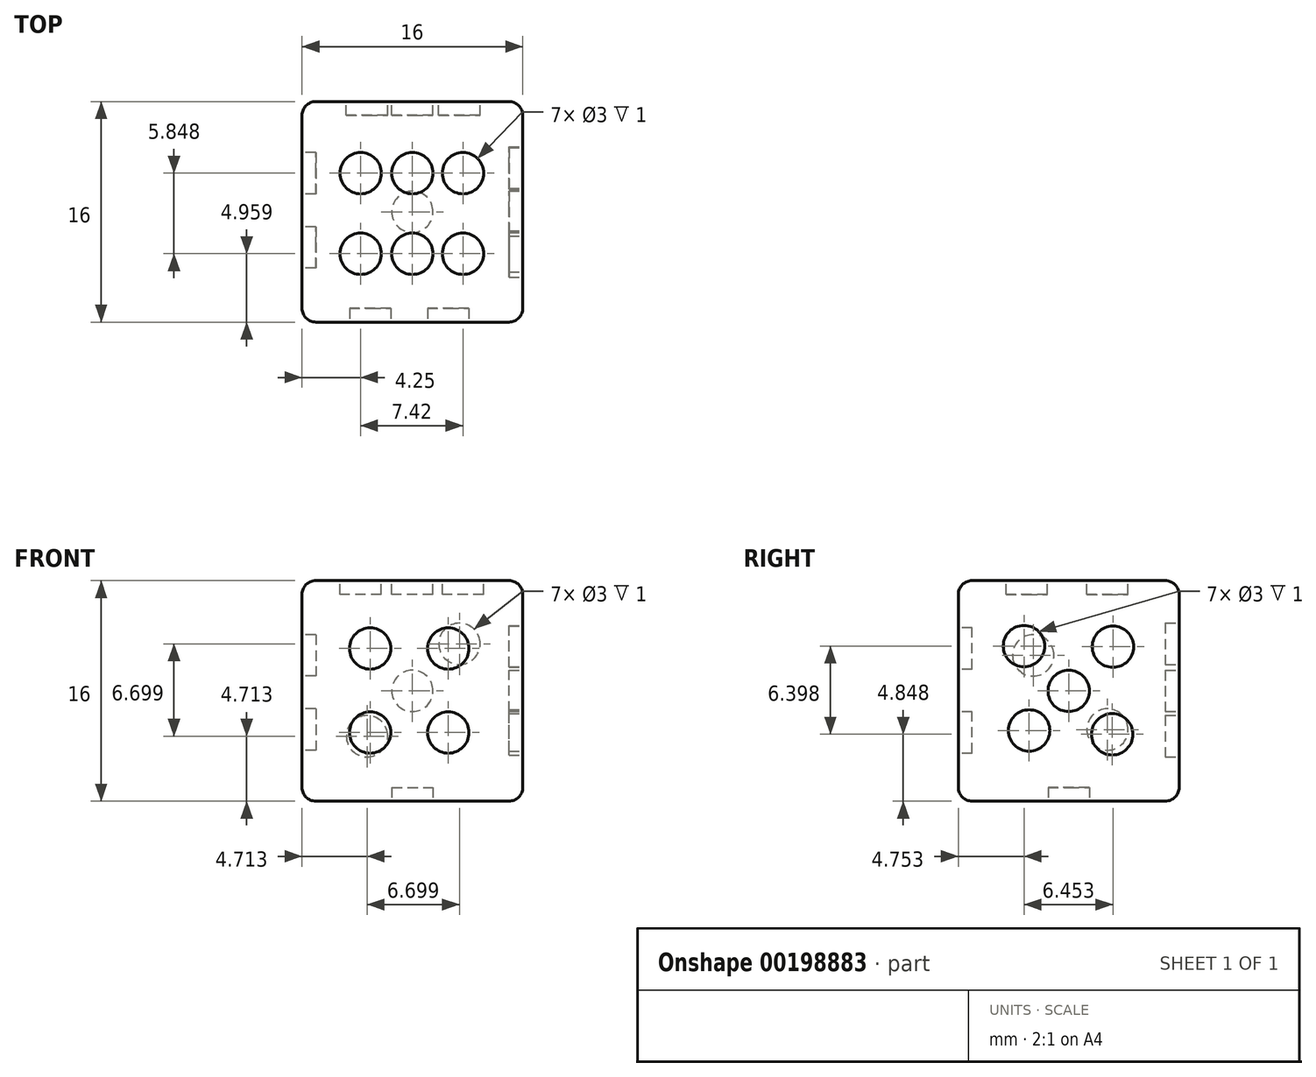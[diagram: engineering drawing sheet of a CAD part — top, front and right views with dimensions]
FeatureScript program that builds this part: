
annotation { "Feature Type Name" : "Feature", "Feature Type Description" : "" }
export const myFeature = defineFeature(function(context is Context, id is Id, definition is map)
    precondition{}
    {
        {
            var Q0;
            Q0=qCreatedBy(makeId("Top.planeOp"),FACE);
            var sketch = newSketch(context, id + "F0", { "sketchPlane" : qUnion([Q0])});
            skLineSegment(sketch, "E0.bottom", {"start": v(8, 8) * mm, "end": v(-8, 8) * mm});
            skLineSegment(sketch, "E0.top", {"start": v(8, -8) * mm, "end": v(-8, -8) * mm});
            skLineSegment(sketch, "E0.left", {"start": v(8, 8) * mm, "end": v(8, -8) * mm});
            skLineSegment(sketch, "E0.right", {"start": v(-8, 8) * mm, "end": v(-8, -8) * mm});
            skPoint(sketch, "E0.middle", {"position": v(0, 0) * mm});
            skSolve(sketch);
        }
        {
            var Q0;
            Q0=makeQuery(id+"F0.imprint","IMPRINT",FACE,{"disambiguationData":[TD([[makeQuery(id+"F0.imprint","IMPRINT",EDGE,{"derivedFrom":sQuery(id+"F0.wireOp",EDGE,"E0.bottom")}),1.0]])]});
            extrude(context, id + "F1", {"entities" : qUnion([Q0]), "depth" : 16 * mm});
        }
        {
            var Q0;
            Q0=makeQuery(id+"F1.opExtrude","CAP_EDGE",EDGE,{"disambiguationData":[OSD([sQuery(id+"F0.wireOp",EDGE,"E0.left")])],"isStart":true});
            var Q1;
            Q1=makeQuery(id+"F1.opExtrude","SWEPT_EDGE",EDGE,{"disambiguationData":[OSD([sQuery(id+"F0.wireOp",EDGE,"E0.bottom"),sQuery(id+"F0.wireOp",EDGE,"E0.left")])]});
            var Q2;
            Q2=makeQuery(id+"F1.opExtrude","SWEPT_EDGE",EDGE,{"disambiguationData":[OSD([sQuery(id+"F0.wireOp",EDGE,"E0.top"),sQuery(id+"F0.wireOp",EDGE,"E0.left")])]});
            var Q3;
            Q3=makeQuery(id+"F1.opExtrude","CAP_EDGE",EDGE,{"disambiguationData":[OSD([sQuery(id+"F0.wireOp",EDGE,"E0.left")])],"isStart":false});
            var Q4;
            Q4=makeQuery(id+"F1.opExtrude","CAP_EDGE",EDGE,{"disambiguationData":[OSD([sQuery(id+"F0.wireOp",EDGE,"E0.right")])],"isStart":false});
            var Q5;
            Q5=makeQuery(id+"F1.opExtrude","CAP_EDGE",EDGE,{"disambiguationData":[OSD([sQuery(id+"F0.wireOp",EDGE,"E0.right")])],"isStart":true});
            var Q6;
            Q6=makeQuery(id+"F1.opExtrude","SWEPT_EDGE",EDGE,{"disambiguationData":[OSD([sQuery(id+"F0.wireOp",EDGE,"E0.top"),sQuery(id+"F0.wireOp",EDGE,"E0.right")])]});
            var Q7;
            Q7=makeQuery(id+"F1.opExtrude","SWEPT_EDGE",EDGE,{"disambiguationData":[OSD([sQuery(id+"F0.wireOp",EDGE,"E0.bottom"),sQuery(id+"F0.wireOp",EDGE,"E0.right")])]});
            var Q8;
            Q8=makeQuery(id+"F1.opExtrude","CAP_EDGE",EDGE,{"disambiguationData":[OSD([sQuery(id+"F0.wireOp",EDGE,"E0.top")])],"isStart":false});
            var Q9;
            Q9=makeQuery(id+"F1.opExtrude","CAP_EDGE",EDGE,{"disambiguationData":[OSD([sQuery(id+"F0.wireOp",EDGE,"E0.top")])],"isStart":true});
            var Q10;
            Q10=makeQuery(id+"F1.opExtrude","SWEPT_FACE",FACE,{"disambiguationData":[OSD([sQuery(id+"F0.wireOp",EDGE,"E0.right")])]});
            var Q11;
            Q11=makeQuery(id+"F1.opExtrude","SWEPT_FACE",FACE,{"disambiguationData":[OSD([sQuery(id+"F0.wireOp",EDGE,"E0.bottom")])]});
            fillet(context, id + "F2", {"entities" : qUnion([Q0, Q1, Q2, Q3, Q4, Q5, Q6, Q7, Q8, Q9, Q10, Q11]), "radius" : 1 * mm, "tangentPropagation" : true, "allowEdgeOverflow" : false});
        }
        {
            var Q0;
            Q0=makeQuery(id+"F1.opExtrude","CAP_FACE",FACE,{"disambiguationData":[OSD([sQuery(id+"F0.wireOp",EDGE,"E0.bottom"),sQuery(id+"F0.wireOp",EDGE,"E0.top"),sQuery(id+"F0.wireOp",EDGE,"E0.left"),sQuery(id+"F0.wireOp",EDGE,"E0.right")])],"isStart":true});
            var sketch = newSketch(context, id + "F3", { "sketchPlane" : qUnion([Q0])});
            skCircle(sketch, "E1", {"center": v(0, 0) * mm, "radius": 1.5 * mm});
            skSolve(sketch);
        }
        {
            var Q0;
            Q0=makeQuery(id+"F1.opExtrude","CAP_FACE",FACE,{"disambiguationData":[OSD([sQuery(id+"F0.wireOp",EDGE,"E0.bottom"),sQuery(id+"F0.wireOp",EDGE,"E0.top"),sQuery(id+"F0.wireOp",EDGE,"E0.left"),sQuery(id+"F0.wireOp",EDGE,"E0.right")])],"isStart":false});
            var sketch = newSketch(context, id + "F4", { "sketchPlane" : qUnion([Q0])});
            skLineSegment(sketch, "E2", {"start": v(-7, 0) * mm, "end": v(7, 0) * mm, "construction": true});
            skLineSegment(sketch, "E3", {"start": v(0, 7) * mm, "end": v(0, -7) * mm, "construction": true});
            skLineSegment(sketch, "E4", {"start": v(7, 2.8) * mm, "end": v(-7, 2.8) * mm, "construction": true});
            skLineSegment(sketch, "E5", {"start": v(7, -3.04) * mm, "end": v(-7, -3.04) * mm, "construction": true});
            skLineSegment(sketch, "E6", {"start": v(3.67, 7) * mm, "end": v(3.67, -7) * mm, "construction": true});
            skLineSegment(sketch, "E7", {"start": v(-3.75, 7) * mm, "end": v(-3.75, -7) * mm, "construction": true});
            skCircle(sketch, "E8", {"center": v(3.67, 2.8) * mm, "radius": 1.5 * mm});
            skCircle(sketch, "E9", {"center": v(0, 2.8) * mm, "radius": 1.5 * mm});
            skCircle(sketch, "E10", {"center": v(-3.75, 2.8) * mm, "radius": 1.5 * mm});
            skCircle(sketch, "E11", {"center": v(3.67, -3.04) * mm, "radius": 1.5 * mm});
            skCircle(sketch, "E12", {"center": v(0, -3.04) * mm, "radius": 1.5 * mm});
            skCircle(sketch, "E13", {"center": v(-3.75, -3.04) * mm, "radius": 1.5 * mm});
            skSolve(sketch);
        }
        {
            var Q0;
            Q0=makeQuery(id+"F4.imprint","IMPRINT",FACE,{"disambiguationData":[TD([[makeQuery(id+"F4.imprint","IMPRINT",EDGE,{"derivedFrom":sQuery(id+"F4.wireOp",EDGE,"E11")}),1.0]])]});
            var Q1;
            Q1=makeQuery(id+"F4.imprint","IMPRINT",FACE,{"disambiguationData":[TD([[makeQuery(id+"F4.imprint","IMPRINT",EDGE,{"derivedFrom":sQuery(id+"F4.wireOp",EDGE,"E8")}),1.0]])]});
            var Q2;
            Q2=makeQuery(id+"F4.imprint","IMPRINT",FACE,{"disambiguationData":[TD([[makeQuery(id+"F4.imprint","IMPRINT",EDGE,{"derivedFrom":sQuery(id+"F4.wireOp",EDGE,"E9")}),1.0]])]});
            var Q3;
            Q3=makeQuery(id+"F4.imprint","IMPRINT",FACE,{"disambiguationData":[TD([[makeQuery(id+"F4.imprint","IMPRINT",EDGE,{"derivedFrom":sQuery(id+"F4.wireOp",EDGE,"E10")}),1.0]])]});
            var Q4;
            Q4=makeQuery(id+"F4.imprint","IMPRINT",FACE,{"disambiguationData":[TD([[makeQuery(id+"F4.imprint","IMPRINT",EDGE,{"derivedFrom":sQuery(id+"F4.wireOp",EDGE,"E13")}),1.0]])]});
            var Q5;
            Q5=makeQuery(id+"F4.imprint","IMPRINT",FACE,{"disambiguationData":[TD([[makeQuery(id+"F4.imprint","IMPRINT",EDGE,{"derivedFrom":sQuery(id+"F4.wireOp",EDGE,"E12")}),1.0]])]});
            extrude(context, id + "F5", {"entities" : qUnion([Q0, Q1, Q2, Q3, Q4, Q5]), "operationType" : NewBodyOperationType.REMOVE, "oppositeDirection" : true, "depth" : 1 * mm});
        }
        {
            var Q0;
            Q0=makeQuery(id+"F3.imprint","IMPRINT",FACE,{"disambiguationData":[TD([[makeQuery(id+"F3.imprint","IMPRINT",EDGE,{"derivedFrom":sQuery(id+"F3.wireOp",EDGE,"E1")}),1.0]])]});
            extrude(context, id + "F6", {"entities" : qUnion([Q0]), "operationType" : NewBodyOperationType.REMOVE, "oppositeDirection" : true, "depth" : 1 * mm});
        }
        {
            var Q0;
            Q0=makeQuery(id+"F1.opExtrude","SWEPT_FACE",FACE,{"disambiguationData":[OSD([sQuery(id+"F0.wireOp",EDGE,"E0.top")])]});
            var sketch = newSketch(context, id + "F7", { "sketchPlane" : qUnion([Q0])});
            skLineSegment(sketch, "E14", {"start": v(7, 8) * mm, "end": v(-7, 8) * mm, "construction": true});
            skLineSegment(sketch, "E15", {"start": v(0, 1) * mm, "end": v(0, 15) * mm, "construction": true});
            skLineSegment(sketch, "E16", {"start": v(-7, 4.98) * mm, "end": v(7, 4.98) * mm, "construction": true});
            skLineSegment(sketch, "E17", {"start": v(7, 11.08) * mm, "end": v(-7, 11.08) * mm, "construction": true});
            skLineSegment(sketch, "E18", {"start": v(-3.06, 1) * mm, "end": v(-3.06, 15) * mm, "construction": true});
            skLineSegment(sketch, "E19", {"start": v(2.6, 1) * mm, "end": v(2.6, 15) * mm, "construction": true});
            skCircle(sketch, "E20", {"center": v(-3.06, 4.98) * mm, "radius": 1.5 * mm});
            skCircle(sketch, "E21", {"center": v(-3.06, 11.08) * mm, "radius": 1.5 * mm});
            skCircle(sketch, "E22", {"center": v(2.6, 11.08) * mm, "radius": 1.5 * mm});
            skCircle(sketch, "E23", {"center": v(2.6, 4.98) * mm, "radius": 1.5 * mm});
            skSolve(sketch);
        }
        {
            var Q0;
            Q0=makeQuery(id+"F7.imprint","IMPRINT",FACE,{"disambiguationData":[TD([[makeQuery(id+"F7.imprint","IMPRINT",EDGE,{"derivedFrom":sQuery(id+"F7.wireOp",EDGE,"E20")}),1.0]])]});
            var Q1;
            Q1=makeQuery(id+"F7.imprint","IMPRINT",FACE,{"disambiguationData":[TD([[makeQuery(id+"F7.imprint","IMPRINT",EDGE,{"derivedFrom":sQuery(id+"F7.wireOp",EDGE,"E23")}),1.0]])]});
            var Q2;
            Q2=makeQuery(id+"F7.imprint","IMPRINT",FACE,{"disambiguationData":[TD([[makeQuery(id+"F7.imprint","IMPRINT",EDGE,{"derivedFrom":sQuery(id+"F7.wireOp",EDGE,"E21")}),1.0]])]});
            var Q3;
            Q3=makeQuery(id+"F7.imprint","IMPRINT",FACE,{"disambiguationData":[TD([[makeQuery(id+"F7.imprint","IMPRINT",EDGE,{"derivedFrom":sQuery(id+"F7.wireOp",EDGE,"E22")}),1.0]])]});
            extrude(context, id + "F8", {"entities" : qUnion([Q0, Q1, Q2, Q3]), "operationType" : NewBodyOperationType.REMOVE, "oppositeDirection" : true, "depth" : 1 * mm});
        }
        {
            var Q0;
            Q0=makeQuery(id+"F1.opExtrude","SWEPT_FACE",FACE,{"disambiguationData":[OSD([sQuery(id+"F0.wireOp",EDGE,"E0.right")])]});
            var sketch = newSketch(context, id + "F9", { "sketchPlane" : qUnion([Q0])});
            skLineSegment(sketch, "E24", {"start": v(-7, 1) * mm, "end": v(7, 15) * mm, "construction": true});
            skLineSegment(sketch, "E25", {"start": v(7, 1) * mm, "end": v(-7, 15) * mm, "construction": true});
            skCircle(sketch, "E26", {"center": v(-2.8, 5.2) * mm, "radius": 1.5 * mm});
            skCircle(sketch, "E27", {"center": v(2.58, 10.58) * mm, "radius": 1.5 * mm});
            skSolve(sketch);
        }
        {
            var Q0;
            Q0=makeQuery(id+"F9.imprint","IMPRINT",FACE,{"disambiguationData":[TD([[makeQuery(id+"F9.imprint","IMPRINT",EDGE,{"derivedFrom":sQuery(id+"F9.wireOp",EDGE,"E26")}),1.0]])]});
            var Q1;
            Q1=makeQuery(id+"F9.imprint","IMPRINT",FACE,{"disambiguationData":[TD([[makeQuery(id+"F9.imprint","IMPRINT",EDGE,{"derivedFrom":sQuery(id+"F9.wireOp",EDGE,"E27")}),1.0]])]});
            extrude(context, id + "F10", {"entities" : qUnion([Q0, Q1]), "operationType" : NewBodyOperationType.REMOVE, "oppositeDirection" : true, "depth" : 1 * mm});
        }
        {
            var Q0;
            Q0=makeQuery(id+"F1.opExtrude","SWEPT_FACE",FACE,{"disambiguationData":[OSD([sQuery(id+"F0.wireOp",EDGE,"E0.bottom")])]});
            var sketch = newSketch(context, id + "F11", { "sketchPlane" : qUnion([Q0])});
            skLineSegment(sketch, "E28", {"start": v(-7, 15) * mm, "end": v(7, 1) * mm, "construction": true});
            skLineSegment(sketch, "E29", {"start": v(-7, 1) * mm, "end": v(7, 15) * mm, "construction": true});
            skCircle(sketch, "E30", {"center": v(0, 8) * mm, "radius": 1.5 * mm});
            skCircle(sketch, "E31", {"center": v(-3.41, 11.41) * mm, "radius": 1.5 * mm});
            skCircle(sketch, "E32", {"center": v(3.29, 4.71) * mm, "radius": 1.5 * mm});
            skSolve(sketch);
        }
        {
            var Q0;
            Q0=makeQuery(id+"F1.opExtrude","SWEPT_FACE",FACE,{"disambiguationData":[OSD([sQuery(id+"F0.wireOp",EDGE,"E0.left")])]});
            var sketch = newSketch(context, id + "F12", { "sketchPlane" : qUnion([Q0])});
            skLineSegment(sketch, "E33", {"start": v(-7, 15) * mm, "end": v(7, 1) * mm, "construction": true});
            skLineSegment(sketch, "E34", {"start": v(-7, 1) * mm, "end": v(7, 15) * mm, "construction": true});
            skCircle(sketch, "E35", {"center": v(0, 8) * mm, "radius": 1.5 * mm});
            skCircle(sketch, "E36", {"center": v(-3.25, 11.25) * mm, "radius": 1.5 * mm});
            skCircle(sketch, "E37", {"center": v(-2.87, 5.13) * mm, "radius": 1.5 * mm});
            skCircle(sketch, "E38", {"center": v(3.2, 11.2) * mm, "radius": 1.5 * mm});
            skCircle(sketch, "E39", {"center": v(3.15, 4.85) * mm, "radius": 1.5 * mm});
            skSolve(sketch);
        }
        {
            var Q0;
            Q0=makeQuery(id+"F12.imprint","IMPRINT",FACE,{"disambiguationData":[TD([[makeQuery(id+"F12.imprint","IMPRINT",EDGE,{"derivedFrom":sQuery(id+"F12.wireOp",EDGE,"E35")}),1.0]])]});
            var Q1;
            Q1=makeQuery(id+"F12.imprint","IMPRINT",FACE,{"disambiguationData":[TD([[makeQuery(id+"F12.imprint","IMPRINT",EDGE,{"derivedFrom":sQuery(id+"F12.wireOp",EDGE,"E39")}),1.0]])]});
            var Q2;
            Q2=makeQuery(id+"F12.imprint","IMPRINT",FACE,{"disambiguationData":[TD([[makeQuery(id+"F12.imprint","IMPRINT",EDGE,{"derivedFrom":sQuery(id+"F12.wireOp",EDGE,"E36")}),1.0]])]});
            var Q3;
            Q3=makeQuery(id+"F12.imprint","IMPRINT",FACE,{"disambiguationData":[TD([[makeQuery(id+"F12.imprint","IMPRINT",EDGE,{"derivedFrom":sQuery(id+"F12.wireOp",EDGE,"E37")}),1.0]])]});
            var Q4;
            Q4=makeQuery(id+"F12.imprint","IMPRINT",FACE,{"disambiguationData":[TD([[makeQuery(id+"F12.imprint","IMPRINT",EDGE,{"derivedFrom":sQuery(id+"F12.wireOp",EDGE,"E38")}),1.0]])]});
            extrude(context, id + "F13", {"entities" : qUnion([Q0, Q1, Q2, Q3, Q4]), "operationType" : NewBodyOperationType.REMOVE, "oppositeDirection" : true, "depth" : 1 * mm});
        }
        {
            var Q0;
            Q0=makeQuery(id+"F11.imprint","IMPRINT",FACE,{"disambiguationData":[TD([[makeQuery(id+"F11.imprint","IMPRINT",EDGE,{"derivedFrom":sQuery(id+"F11.wireOp",EDGE,"E31")}),1.0]])]});
            var Q1;
            Q1=makeQuery(id+"F11.imprint","IMPRINT",FACE,{"disambiguationData":[TD([[makeQuery(id+"F11.imprint","IMPRINT",EDGE,{"derivedFrom":sQuery(id+"F11.wireOp",EDGE,"E32")}),1.0]])]});
            var Q2;
            Q2=makeQuery(id+"F11.imprint","IMPRINT",FACE,{"disambiguationData":[TD([[makeQuery(id+"F11.imprint","IMPRINT",EDGE,{"derivedFrom":sQuery(id+"F11.wireOp",EDGE,"E30")}),1.0]])]});
            extrude(context, id + "F14", {"entities" : qUnion([Q0, Q1, Q2]), "operationType" : NewBodyOperationType.REMOVE, "oppositeDirection" : true, "depth" : 1 * mm});
        }
    });
